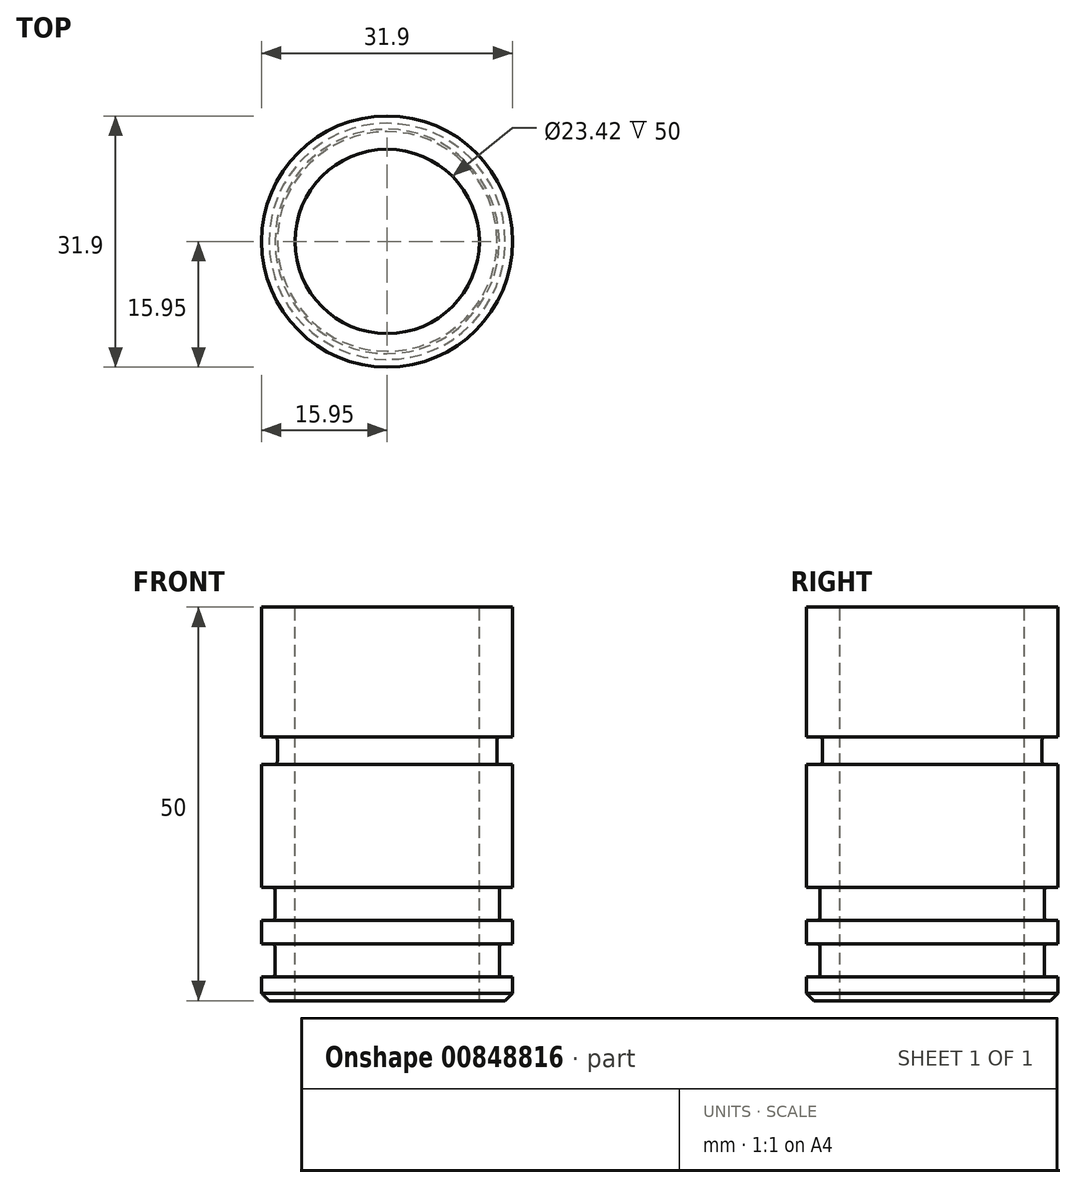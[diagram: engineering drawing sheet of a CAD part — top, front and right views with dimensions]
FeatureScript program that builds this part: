
annotation { "Feature Type Name" : "Feature", "Feature Type Description" : "" }
export const myFeature = defineFeature(function(context is Context, id is Id, definition is map)
    precondition{}
    {
        {
            var Q0;
            Q0=qCreatedBy(makeId("Top.planeOp"),FACE);
            var sketch = newSketch(context, id + "F0", { "sketchPlane" : qUnion([Q0])});
            skCircle(sketch, "E0", {"center": v(0, 0) * mm, "radius": 15.95 * mm});
            skSolve(sketch);
        }
        {
            var Q0;
            Q0=makeQuery(id+"F0.imprint","IMPRINT",FACE,{"disambiguationData":[TD([[makeQuery(id+"F0.imprint","IMPRINT",EDGE,{"derivedFrom":sQuery(id+"F0.wireOp",EDGE,"E0")}),1.0]])]});
            extrude(context, id + "F1", {"entities" : qUnion([Q0]), "depth" : 50 * mm, "offsetDistance" : 25 * mm});
        }
        {
            var Q0;
            Q0=qCreatedBy(makeId("Front.planeOp"),FACE);
            var sketch = newSketch(context, id + "F2", { "sketchPlane" : qUnion([Q0])});
            skLineSegment(sketch, "E1.bottom", {"start": v(15.95, 3) * mm, "end": v(14.25, 3) * mm});
            skLineSegment(sketch, "E1.top", {"start": v(15.95, 7.2) * mm, "end": v(14.25, 7.2) * mm});
            skLineSegment(sketch, "E1.left", {"start": v(15.95, 3) * mm, "end": v(15.95, 7.2) * mm});
            skLineSegment(sketch, "E1.right", {"start": v(14.25, 3) * mm, "end": v(14.25, 7.2) * mm});
            skLineSegment(sketch, "E2.bottom", {"start": v(15.95, 10.2) * mm, "end": v(14.25, 10.2) * mm});
            skLineSegment(sketch, "E2.top", {"start": v(15.95, 14.4) * mm, "end": v(14.25, 14.4) * mm});
            skLineSegment(sketch, "E2.left", {"start": v(15.95, 10.2) * mm, "end": v(15.95, 14.4) * mm});
            skLineSegment(sketch, "E2.right", {"start": v(14.25, 10.2) * mm, "end": v(14.25, 14.4) * mm});
            skLineSegment(sketch, "E3", {"start": v(15.95, 7.2) * mm, "end": v(15.95, 10.2) * mm, "construction": true});
            skSolve(sketch);
        }
        {
            var Q0;
            Q0=qCreatedBy(makeId("Front.planeOp"),FACE);
            var sketch = newSketch(context, id + "F3", { "sketchPlane" : qUnion([Q0])});
            skLineSegment(sketch, "E4", {"start": v(0, 65.77) * mm, "end": v(0, 0) * mm, "construction": true});
            skSolve(sketch);
        }
        {
            var Q0;
            Q0 = qSketchRegion(id + "F2", true);
            var Q1;
            Q1=sQuery(id+"F3.wireOp",EDGE,"E4");
            revolve(context, id + "F4", {"operationType" : NewBodyOperationType.REMOVE, "surfaceOperationType" : NewSurfaceOperationType.NEW, "entities" : qUnion([Q0]), "axis" : qUnion([Q1]), "revolveType" : RevolveType.FULL, "oppositeDirection" : true});
        }
        {
            var Q0;
            Q0=makeQuery(id+"F4.boolean.opBoolean","COPY",EDGE,{"derivedFrom":makeQuery(id+"F4.opRevolve","SWEPT_EDGE",EDGE,{"disambiguationData":[OSD([sQuery(id+"F2.wireOp",EDGE,"E1.bottom"),sQuery(id+"F2.wireOp",EDGE,"E1.right")])]})});
            var Q1;
            Q1=makeQuery(id+"F4.boolean.opBoolean","COPY",EDGE,{"derivedFrom":makeQuery(id+"F4.opRevolve","SWEPT_EDGE",EDGE,{"disambiguationData":[OSD([sQuery(id+"F2.wireOp",EDGE,"E1.top"),sQuery(id+"F2.wireOp",EDGE,"E1.right")])]})});
            var Q2;
            Q2=makeQuery(id+"F4.boolean.opBoolean","COPY",EDGE,{"derivedFrom":makeQuery(id+"F4.opRevolve","SWEPT_EDGE",EDGE,{"disambiguationData":[OSD([sQuery(id+"F2.wireOp",EDGE,"E2.top"),sQuery(id+"F2.wireOp",EDGE,"E2.right")])]})});
            var Q3;
            Q3=makeQuery(id+"F4.boolean.opBoolean","COPY",EDGE,{"derivedFrom":makeQuery(id+"F4.opRevolve","SWEPT_EDGE",EDGE,{"disambiguationData":[OSD([sQuery(id+"F2.wireOp",EDGE,"E2.bottom"),sQuery(id+"F2.wireOp",EDGE,"E2.right")])]})});
            fillet(context, id + "F5", {"entities" : qUnion([Q0, Q1, Q2, Q3]), "radius" : .4 * mm, "tangentPropagation" : true, "allowEdgeOverflow" : false});
        }
        {
            var Q0;
            Q0=qCreatedBy(makeId("Front.planeOp"),FACE);
            var sketch = newSketch(context, id + "F6", { "sketchPlane" : qUnion([Q0])});
            skLineSegment(sketch, "E5.bottom", {"start": v(15.95, 30) * mm, "end": v(13.95, 30) * mm});
            skLineSegment(sketch, "E5.top", {"start": v(15.95, 33.5) * mm, "end": v(13.95, 33.5) * mm});
            skLineSegment(sketch, "E5.left", {"start": v(15.95, 30) * mm, "end": v(15.95, 33.5) * mm});
            skLineSegment(sketch, "E5.right", {"start": v(13.95, 30) * mm, "end": v(13.95, 33.5) * mm});
            skSolve(sketch);
        }
        {
            var Q0;
            Q0 = qSketchRegion(id + "F6", true);
            var Q1;
            {var subQ0=sQuery(id+"F0.wireOp",EDGE,"E0");Q1=makeQuery(id+"F4.boolean.opBoolean","SPLIT",FACE,{"disambiguationData":[TD([makeQuery(id+"F1.opExtrude","CAP_FACE",FACE,{"disambiguationData":[OSD([subQ0])],"isStart":false})])],"derivedFrom":makeQuery(id+"F1.opExtrude","SWEPT_FACE",FACE,{"disambiguationData":[OSD([subQ0])]})});}
            revolve(context, id + "F7", {"operationType" : NewBodyOperationType.REMOVE, "surfaceOperationType" : NewSurfaceOperationType.NEW, "entities" : qUnion([Q0]), "axis" : qUnion([Q1]), "revolveType" : RevolveType.FULL, "oppositeDirection" : true});
        }
        {
            var Q0;
            Q0=makeQuery(id+"F7.boolean.opBoolean","COPY",EDGE,{"derivedFrom":makeQuery(id+"F7.opRevolve","SWEPT_EDGE",EDGE,{"disambiguationData":[OSD([sQuery(id+"F6.wireOp",EDGE,"E5.bottom"),sQuery(id+"F6.wireOp",EDGE,"E5.right")])]})});
            var Q1;
            Q1=makeQuery(id+"F7.boolean.opBoolean","COPY",EDGE,{"derivedFrom":makeQuery(id+"F7.opRevolve","SWEPT_EDGE",EDGE,{"disambiguationData":[OSD([sQuery(id+"F6.wireOp",EDGE,"E5.top"),sQuery(id+"F6.wireOp",EDGE,"E5.right")])]})});
            fillet(context, id + "F8", {"entities" : qUnion([Q0, Q1]), "radius" : .4 * mm, "tangentPropagation" : true, "allowEdgeOverflow" : false});
        }
        {
            var Q0;
            Q0=makeQuery(id+"F1.opExtrude","CAP_FACE",FACE,{"disambiguationData":[OSD([sQuery(id+"F0.wireOp",EDGE,"E0")])],"isStart":false});
            var sketch = newSketch(context, id + "F9", { "sketchPlane" : qUnion([Q0])});
            skCircle(sketch, "E6", {"center": v(0, 0) * mm, "radius": 11.7 * mm});
            skSolve(sketch);
        }
        {
            var Q0;
            Q0 = qSketchRegion(id + "F9", true);
            extrude(context, id + "F10", {"entities" : qUnion([Q0]), "operationType" : NewBodyOperationType.REMOVE, "endBound" : BoundingType.THROUGH_ALL, "oppositeDirection" : true, "depth" : 25 * mm, "offsetDistance" : 25 * mm});
        }
        {
            var Q0;
            Q0=qCreatedBy(makeId("Front.planeOp"),FACE);
            var sketch = newSketch(context, id + "F11", { "sketchPlane" : qUnion([Q0])});
            skLineSegment(sketch, "E7", {"start": v(15.95, 0) * mm, "end": v(15.95, 0.95) * mm});
            skLineSegment(sketch, "E8", {"start": v(15.95, 0.95) * mm, "end": v(15, 0) * mm});
            skLineSegment(sketch, "E9", {"start": v(15, 0) * mm, "end": v(15.95, 0) * mm});
            skSolve(sketch);
        }
        {
            var Q0;
            Q0 = qSketchRegion(id + "F11", true);
            var Q1;
            Q1=makeQuery(id+"F10.boolean.opBoolean","COPY",FACE,{"derivedFrom":makeQuery(id+"F10.opExtrude","SWEPT_FACE",FACE,{"disambiguationData":[OSD([sQuery(id+"F9.wireOp",EDGE,"E6")])]})});
            revolve(context, id + "F12", {"operationType" : NewBodyOperationType.REMOVE, "surfaceOperationType" : NewSurfaceOperationType.NEW, "entities" : qUnion([Q0]), "axis" : qUnion([Q1]), "revolveType" : RevolveType.FULL, "oppositeDirection" : true});
        }
    });
